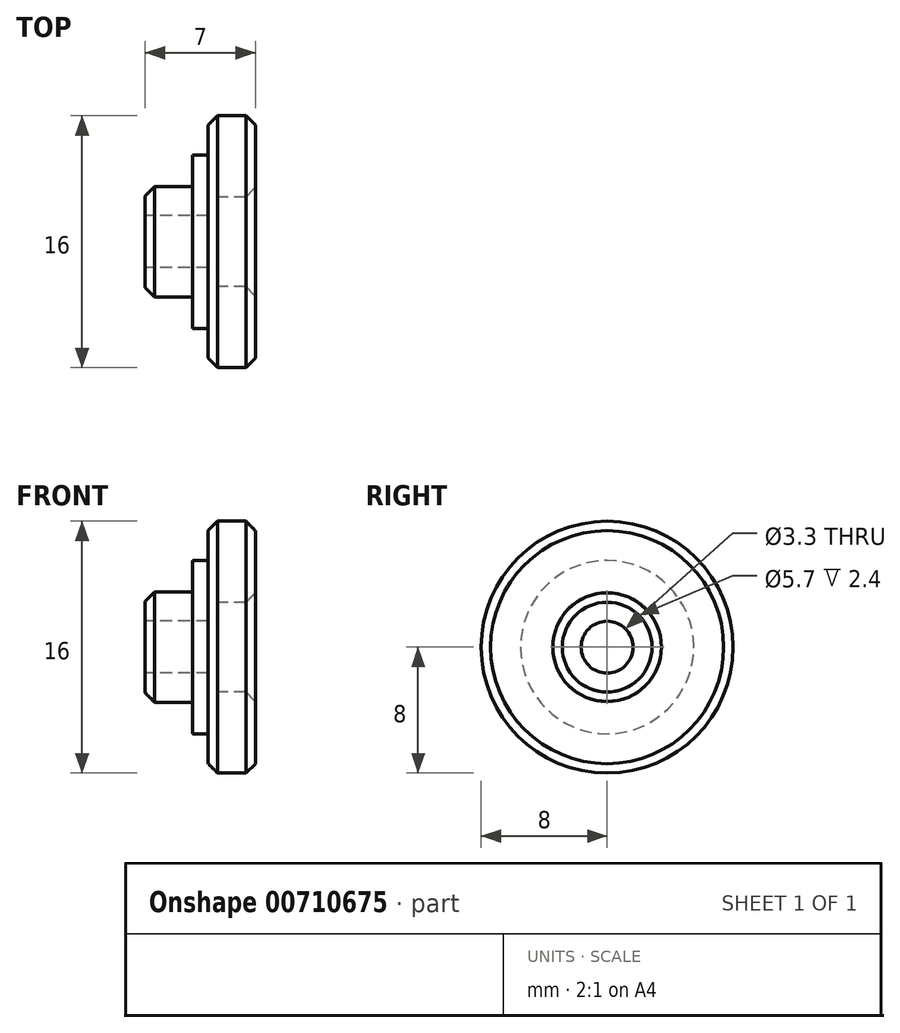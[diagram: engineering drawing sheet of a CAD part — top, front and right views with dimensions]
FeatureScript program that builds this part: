
annotation { "Feature Type Name" : "Feature", "Feature Type Description" : "" }
export const myFeature = defineFeature(function(context is Context, id is Id, definition is map)
    precondition{}
    {
        {
            var Q0;
            Q0=qCreatedBy(makeId("Front.planeOp"),FACE);
            var sketch = newSketch(context, id + "F0", { "sketchPlane" : qUnion([Q0])});
            skLineSegment(sketch, "E0", {"start": v(0, 1.65) * mm, "end": v(4, 1.65) * mm});
            skLineSegment(sketch, "E1", {"start": v(4, 1.65) * mm, "end": v(4, 2.85) * mm});
            skLineSegment(sketch, "E2", {"start": v(4, 2.85) * mm, "end": v(7, 2.85) * mm});
            skLineSegment(sketch, "E3", {"start": v(7, 2.85) * mm, "end": v(7, 8) * mm});
            skLineSegment(sketch, "E4", {"start": v(7, 8) * mm, "end": v(4, 8) * mm});
            skLineSegment(sketch, "E5", {"start": v(0, 3.5) * mm, "end": v(0, 1.65) * mm});
            skLineSegment(sketch, "E6", {"start": v(0, 0) * mm, "end": v(8.14, 0) * mm, "construction": true});
            skLineSegment(sketch, "E7", {"start": v(4, 8) * mm, "end": v(4, 5.5) * mm});
            skLineSegment(sketch, "E8", {"start": v(4, 5.5) * mm, "end": v(3, 5.5) * mm});
            skLineSegment(sketch, "E9", {"start": v(3, 5.5) * mm, "end": v(3, 3.5) * mm});
            skLineSegment(sketch, "E10", {"start": v(3, 3.5) * mm, "end": v(0, 3.5) * mm});
            skSolve(sketch);
        }
        {
            var Q0;
            Q0=makeQuery(id+"F0.imprint","IMPRINT",FACE,{"disambiguationData":[TD([[makeQuery(id+"F0.imprint","IMPRINT",EDGE,{"derivedFrom":sQuery(id+"F0.wireOp",EDGE,"E0")}),1.0]])]});
            var Q1;
            Q1=sQuery(id+"F0.wireOp",EDGE,"E6");
            revolve(context, id + "F1", {"surfaceOperationType" : NewSurfaceOperationType.NEW, "entities" : qUnion([Q0]), "axis" : qUnion([Q1]), "revolveType" : RevolveType.FULL});
        }
        {
            var Q0;
            Q0=makeQuery(id+"F1.opRevolve","SWEPT_EDGE",EDGE,{"disambiguationData":[OSD([sQuery(id+"F0.wireOp",EDGE,"E3"),sQuery(id+"F0.wireOp",EDGE,"E4")])]});
            var Q1;
            Q1=makeQuery(id+"F1.opRevolve","SWEPT_EDGE",EDGE,{"disambiguationData":[OSD([sQuery(id+"F0.wireOp",EDGE,"E4"),sQuery(id+"F0.wireOp",EDGE,"E7")])]});
            var Q2;
            Q2=makeQuery(id+"F1.opRevolve","SWEPT_EDGE",EDGE,{"disambiguationData":[OSD([sQuery(id+"F0.wireOp",EDGE,"E2"),sQuery(id+"F0.wireOp",EDGE,"E3")])]});
            var Q3;
            Q3=makeQuery(id+"F1.opRevolve","SWEPT_EDGE",EDGE,{"disambiguationData":[OSD([sQuery(id+"F0.wireOp",EDGE,"E5"),sQuery(id+"F0.wireOp",EDGE,"E10")])]});
            chamfer(context, id + "F2", {"entities" : qUnion([Q0, Q1, Q2, Q3]), "width" : 0.6 * mm, "tangentPropagation" : true});
        }
    });
